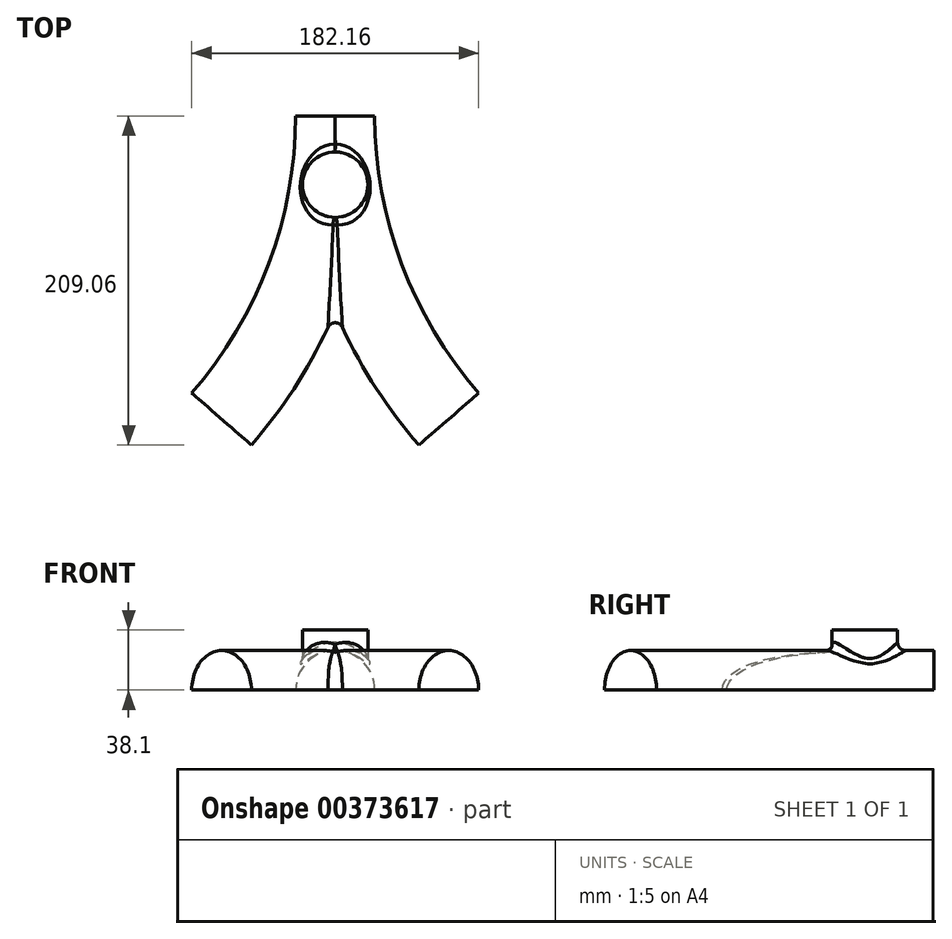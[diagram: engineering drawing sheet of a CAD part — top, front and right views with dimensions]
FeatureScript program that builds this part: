
annotation { "Feature Type Name" : "Feature", "Feature Type Description" : "" }
export const myFeature = defineFeature(function(context is Context, id is Id, definition is map)
    precondition{}
    {
        {
            var Q0;
            Q0=qCreatedBy(makeId("Top.planeOp"),FACE);
            var sketch = newSketch(context, id + "F0", { "sketchPlane" : qUnion([Q0])});
            skLineSegment(sketch, "E0", {"start": v(0, 0) * mm, "end": v(0, -43.68) * mm});
            skCircle(sketch, "E1", {"center": v(0, -43.68) * mm, "radius": 20.77 * mm});
            skSolve(sketch);
        }
        {
            var Q0;
            {var subQ0=sQuery(id+"F0.wireOp",EDGE,"E1");Q0=makeQuery(id+"F0.imprint","IMPRINT",FACE,{"disambiguationData":[TD([[makeQuery(id+"F0.imprint","IMPRINT",EDGE,{"derivedFrom":subQ0}),1.0]])]});}
            extrude(context, id + "F1", {"entities" : qUnion([Q0]), "depth" : 38.1 * mm});
        }
        {
            var Q0;
            Q0=qCreatedBy(makeId("Top.planeOp"),FACE);
            var sketch = newSketch(context, id + "F2", { "sketchPlane" : qUnion([Q0])});
            skArc(sketch, "E2", {"start": v(-72.14, -192.55) * mm, "mid": v(-18.63, -102.8) * mm, "end": v(0, 0) * mm});
            skLineSegment(sketch, "E3", {"start": v(0, 0) * mm, "end": v(0, -167.15) * mm, "construction": true});
            skArc(sketch, "E4.MirrorCS", {"start": v(72.14, -192.55) * mm, "mid": v(18.63, -102.8) * mm, "end": v(0, 0) * mm});
            skSolve(sketch);
        }
        {
            var Q0;
            Q0=qCreatedBy(makeId("Front.planeOp"),FACE);
            var sketch = newSketch(context, id + "F3", { "sketchPlane" : qUnion([Q0])});
            skLineSegment(sketch, "E5", {"start": v(25.13, 0) * mm, "end": v(-25.13, 0) * mm});
            skArc(sketch, "E6", {"start": v(25.13, 0) * mm, "mid": v(0, 25.13) * mm, "end": v(-25.13, 0) * mm});
            skSolve(sketch);
        }
        {
            var Q0;
            Q0=makeQuery(id+"F3.imprint","IMPRINT",FACE,{"disambiguationData":[TD([[makeQuery(id+"F3.imprint","IMPRINT",EDGE,{"derivedFrom":sQuery(id+"F3.wireOp",EDGE,"E5")}),-1.0]])]});
            var Q1;
            Q1=sQuery(id+"F2.wireOp",EDGE,"E2");
            sweep(context, id + "F4", {"operationType" : NewBodyOperationType.ADD, "profiles" : qUnion([Q0]), "path" : qUnion([Q1])});
        }
        {
            var Q0;
            Q0=makeQuery(id+"F4.opSweep","CAP_FACE",FACE,{"disambiguationData":[OSD([sQuery(id+"F2.wireOp",VERTEX,"E2.end"),sQuery(id+"F3.wireOp",EDGE,"E5"),sQuery(id+"F3.wireOp",EDGE,"E6")])],"isStart":true});
            var Q1;
            Q1=sQuery(id+"F2.wireOp",EDGE,"E4.MirrorCS");
            sweep(context, id + "F5", {"operationType" : NewBodyOperationType.ADD, "profiles" : qUnion([Q0]), "path" : qUnion([Q1])});
        }
        {
            var Q0;
            Q0=makeQuery(id+"F5.boolean.opBoolean","INTERSECT",EDGE,{"derivedFrom":[makeQuery(id+"F1.opExtrude","SWEPT_FACE",FACE,{"disambiguationData":[OSD([sQuery(id+"F0.wireOp",EDGE,"E1")])]}),makeQuery(id+"F5.opSweep","SWEPT_FACE",FACE,{"disambiguationData":[OSD([sQuery(id+"F2.wireOp",VERTEX,"E2.end"),sQuery(id+"F2.wireOp",EDGE,"E4.MirrorCS"),sQuery(id+"F3.wireOp",EDGE,"E6")])]})]});
            var Q1;
            Q1=makeQuery(id+"F4.boolean.opBoolean","INTERSECT",EDGE,{"derivedFrom":[makeQuery(id+"F1.opExtrude","SWEPT_FACE",FACE,{"disambiguationData":[OSD([sQuery(id+"F0.wireOp",EDGE,"E1")])]}),makeQuery(id+"F4.opSweep","SWEPT_FACE",FACE,{"disambiguationData":[OSD([sQuery(id+"F2.wireOp",EDGE,"E2"),sQuery(id+"F3.wireOp",EDGE,"E6")])]})]});
            var Q2;
            {var subQ0=sQuery(id+"F3.wireOp",EDGE,"E6");Q2=makeQuery(id+"F5.boolean.opBoolean","INTERSECT",EDGE,{"disambiguationData":[OD(1.0)],"derivedFrom":[makeQuery(id+"F4.opSweep","SWEPT_FACE",FACE,{"disambiguationData":[OSD([sQuery(id+"F2.wireOp",EDGE,"E2"),subQ0])]}),makeQuery(id+"F5.opSweep","SWEPT_FACE",FACE,{"disambiguationData":[OSD([sQuery(id+"F2.wireOp",VERTEX,"E2.end"),sQuery(id+"F2.wireOp",EDGE,"E4.MirrorCS"),subQ0])]})]});}
            fillet(context, id + "F6", {"entities" : qUnion([Q0, Q1, Q2]), "radius" : 5.08 * mm, "tangentPropagation" : true, "allowEdgeOverflow" : false});
        }
    });
